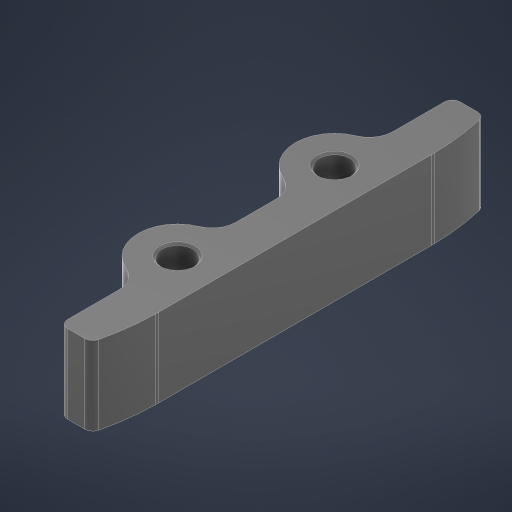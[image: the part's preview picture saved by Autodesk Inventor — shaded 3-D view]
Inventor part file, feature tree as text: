
AUTODESK INVENTOR PART (.ipt)
format: ipt  version: 2025 (Build 290162010, 162A)  size: 232,960 bytes
history: native  units: mm
features: fillet x3, extrude x1, chamfer x1, sketch x1
ambient origin geometry x8: Origin, YZ Plane, XZ Plane, XY Plane, X Axis, Y Axis, Z Axis, Center Point
bodies: Solid1 (feature_tree)
feature tree (6):
  extrude  "Extrusion1"  Depth=20.0mm
  fillet  "Fillet1"  Radius=4.0mm
  fillet  "Fillet2"  Radius=10.0mm
  fillet  "Fillet3"  Radius=10.0mm
  chamfer  "Chamfer1"  Distance=5.0mm
  sketch  "Sketch1"  dims[d0=4.0mm d1=20.0mm d2=4.0mm d3=10.0mm d4=10.0mm d5=5.0mm d6=25.0mm d7=25.0mm d8=10.0mm d9=4.0mm d10=10.0mm d11=4.0mm d12=17.5mm d13=17.5mm d14=30.0mm d15=30.0mm d16=10.0mm d17=0.0mm d18=3.0mm d19=1.0mm d20=25.0mm d21=0.25mm d22=2.0mm d23=45.0deg]
